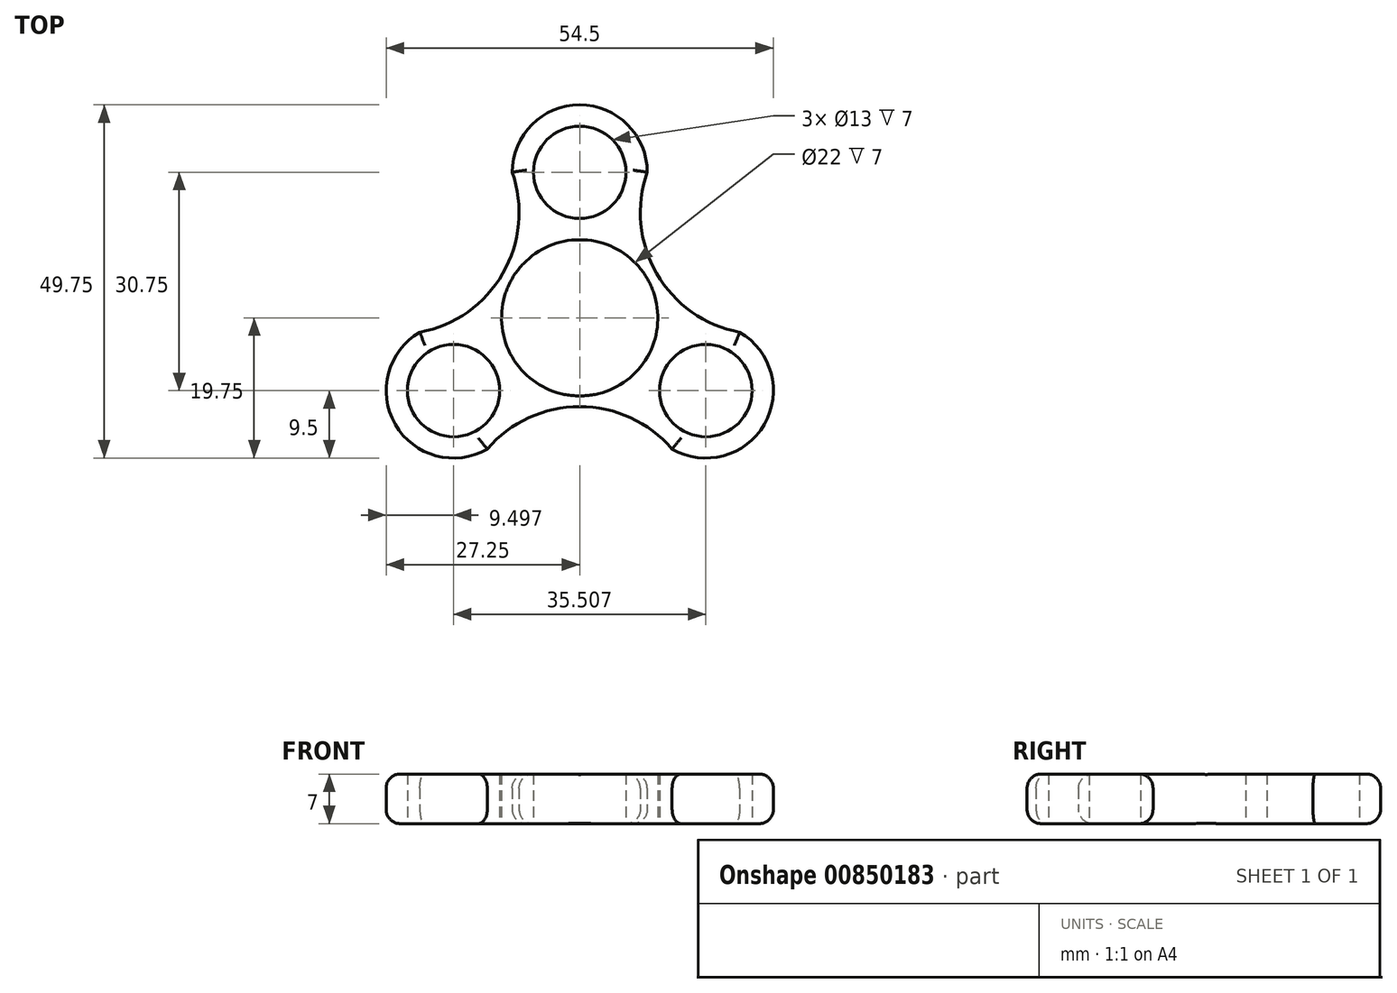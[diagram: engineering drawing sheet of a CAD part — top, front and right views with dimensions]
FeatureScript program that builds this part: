
annotation { "Feature Type Name" : "Feature", "Feature Type Description" : "" }
export const myFeature = defineFeature(function(context is Context, id is Id, definition is map)
    precondition{}
    {
        {
            var Q0;
            Q0=qCreatedBy(makeId("Top.planeOp"),FACE);
            var sketch = newSketch(context, id + "F0", { "sketchPlane" : qUnion([Q0])});
            skCircle(sketch, "E0", {"center": v(0, 0) * mm, "radius": 11 * mm});
            skCircle(sketch, "E1", {"center": v(0, 20.5) * mm, "radius": 6.5 * mm});
            skArc(sketch, "E2.0", {"start": v(9.5, 20.5) * mm, "mid": v(0, 30) * mm, "end": v(-9.5, 20.5) * mm});
            skCircle(sketch, "E3.1.1", {"center": v(-17.75, -10.25) * mm, "radius": 6.5 * mm});
            skCircle(sketch, "E3.2.1", {"center": v(17.75, -10.25) * mm, "radius": 6.5 * mm});
            skLineSegment(sketch, "E4", {"start": v(9.53, 5.5) * mm, "end": v(12.12, 7) * mm});
            skPoint(sketch, "E5", {"position": v(10.83, 6.25) * mm});
            skLineSegment(sketch, "E6.MirrorCS", {"start": v(17.75, -10.25) * mm, "end": v(18.88, -3.85) * mm});
            skLineSegment(sketch, "E7.MirrorCS", {"start": v(17.75, -10.25) * mm, "end": v(21, -4.62) * mm});
            skArc(sketch, "E8", {"start": v(9.5, 20.5) * mm, "mid": v(10.83, 6.25) * mm, "end": v(22.5, -2.02) * mm});
            skArc(sketch, "E9.1.0", {"start": v(-22.5, -2.02) * mm, "mid": v(-10.83, 6.25) * mm, "end": v(-9.5, 20.5) * mm});
            skArc(sketch, "E9.2.0", {"start": v(13, -18.48) * mm, "mid": v(0, -12.5) * mm, "end": v(-13, -18.48) * mm});
            skArc(sketch, "E10.trimOffspring", {"start": v(13, -18.48) * mm, "mid": v(25.98, -15) * mm, "end": v(22.5, -2.02) * mm});
            skArc(sketch, "E11.trimOffspring", {"start": v(-13.91, -1.56) * mm, "mid": v(-13.3, -4.37) * mm, "end": v(-12.12, -7) * mm});
            skArc(sketch, "E12.trimOffspring", {"start": v(-22.5, -2.02) * mm, "mid": v(-25.98, -15) * mm, "end": v(-13, -18.48) * mm});
            skLineSegment(sketch, "E13.trimOffspring", {"start": v(19.36, -1.12) * mm, "end": v(19.4, -0.9) * mm});
            skSolve(sketch);
        }
        {
            var Q0;
            {var subQ0=sQuery(id+"F0.wireOp",EDGE,"0f1f7083-71ca-4fd1-acfb-ab530d3e9b21.1.0");var subQ1=sQuery(id+"F0.wireOp",EDGE,"457ceb27-7422-4ba8-bad2-b165804d5d78.0");var subQ2=makeQuery(id+"F0.imprint","INTERSECT",VERTEX,{"derivedFrom":[subQ1,subQ0]});Q0=makeQuery(id+"F0.imprint","IMPRINT",FACE,{"disambiguationData":[TD([[makeQuery(id+"F0.imprint","IMPRINT",EDGE,{"disambiguationData":[TD([[subQ2,-1.0]])],"derivedFrom":subQ0}),-1.0]])]});}
            var Q1;
            {var subQ3=sQuery(id+"F0.wireOp",EDGE,"crWTvBME-xT62-r7Xz-G13u-5dXDQIS6QdV6");var subQ5=sQuery(id+"F0.wireOp",EDGE,"E1");var subQ6=makeQuery(id+"F0.imprint","INTERSECT",VERTEX,{"derivedFrom":[subQ5,subQ3]});Q1=makeQuery(id+"F0.imprint","IMPRINT",FACE,{"disambiguationData":[TD([[makeQuery(id+"F0.imprint","IMPRINT",EDGE,{"disambiguationData":[TD([[subQ6,1.0]])],"derivedFrom":subQ5}),-1.0]])]});}
            var Q2;
            {var subQ4=sQuery(id+"F0.wireOp",EDGE,"E1");var subQ7=sQuery(id+"F0.wireOp",EDGE,"crWTvBME-xT62-r7Xz-G13u-5dXDQIS6QdV6");var subQ9=makeQuery(id+"F0.imprint","INTERSECT",VERTEX,{"derivedFrom":[subQ4,subQ7]});Q2=makeQuery(id+"F0.imprint","IMPRINT",FACE,{"disambiguationData":[TD([[makeQuery(id+"F0.imprint","IMPRINT",EDGE,{"disambiguationData":[TD([[subQ9,-1.0]])],"derivedFrom":subQ4}),-1.0]])]});}
            var Q3;
            {var subQ0=sQuery(id+"F0.wireOp",EDGE,"FCme8Fqz-nV7u-H02u-gcTn-oEhTSx07MFKY");var subQ3=sQuery(id+"F0.wireOp",EDGE,"E2.0");var subQ5=makeQuery(id+"F0.imprint","INTERSECT",VERTEX,{"derivedFrom":[subQ3,subQ0]});Q3=makeQuery(id+"F0.imprint","IMPRINT",FACE,{"disambiguationData":[TD([[makeQuery(id+"F0.imprint","IMPRINT",EDGE,{"disambiguationData":[TD([[subQ5,1.0]])],"derivedFrom":subQ3}),-1.0]])]});}
            var Q4;
            {var subQ0=sQuery(id+"F0.wireOp",EDGE,"crWTvBME-xT62-r7Xz-G13u-5dXDQIS6QdV6");var subQ1=sQuery(id+"F0.wireOp",EDGE,"E0");var subQ2=makeQuery(id+"F0.imprint","INTERSECT",VERTEX,{"derivedFrom":[subQ1,subQ0]});Q4=makeQuery(id+"F0.imprint","IMPRINT",FACE,{"disambiguationData":[TD([[makeQuery(id+"F0.imprint","IMPRINT",EDGE,{"disambiguationData":[TD([[subQ2,1.0]])],"derivedFrom":subQ1}),-1.0]])]});}
            var Q5;
            {var subQ3=sQuery(id+"F0.wireOp",EDGE,"crWTvBME-xT62-r7Xz-G13u-5dXDQIS6QdV6");var subQ7=sQuery(id+"F0.wireOp",EDGE,"E0");var subQ9=makeQuery(id+"F0.imprint","INTERSECT",VERTEX,{"derivedFrom":[subQ7,subQ3]});Q5=makeQuery(id+"F0.imprint","IMPRINT",FACE,{"disambiguationData":[TD([[makeQuery(id+"F0.imprint","IMPRINT",EDGE,{"disambiguationData":[TD([[subQ9,-1.0]])],"derivedFrom":subQ7}),-1.0]])]});}
            var Q6;
            {var subQ0=sQuery(id+"F0.wireOp",EDGE,"0f1f7083-71ca-4fd1-acfb-ab530d3e9b21.1.0");var subQ1=sQuery(id+"F0.wireOp",EDGE,"457ceb27-7422-4ba8-bad2-b165804d5d78.0");var subQ2=makeQuery(id+"F0.imprint","INTERSECT",VERTEX,{"derivedFrom":[subQ1,subQ0]});Q6=makeQuery(id+"F0.imprint","IMPRINT",FACE,{"disambiguationData":[TD([[makeQuery(id+"F0.imprint","IMPRINT",EDGE,{"disambiguationData":[TD([[subQ2,-1.0]])],"derivedFrom":subQ1}),-1.0]])]});}
            var Q7;
            Q7=makeQuery(id+"F0.imprint","IMPRINT",FACE,{"disambiguationData":[TD([[makeQuery(id+"F0.imprint","IMPRINT",EDGE,{"derivedFrom":sQuery(id+"F0.wireOp",EDGE,"E3.1.1")}),-1.0]])]});
            var Q8;
            {var subQ0=sQuery(id+"F0.wireOp",EDGE,"0f1f7083-71ca-4fd1-acfb-ab530d3e9b21.2.0");var subQ1=sQuery(id+"F0.wireOp",EDGE,"457ceb27-7422-4ba8-bad2-b165804d5d78.0");var subQ2=makeQuery(id+"F0.imprint","INTERSECT",VERTEX,{"derivedFrom":[subQ1,subQ0]});Q8=makeQuery(id+"F0.imprint","IMPRINT",FACE,{"disambiguationData":[TD([[makeQuery(id+"F0.imprint","IMPRINT",EDGE,{"disambiguationData":[TD([[subQ2,1.0]])],"derivedFrom":subQ1}),-1.0]])]});}
            var Q9;
            {var subQ0=sQuery(id+"F0.wireOp",EDGE,"0f1f7083-71ca-4fd1-acfb-ab530d3e9b21.2.0");var subQ1=sQuery(id+"F0.wireOp",EDGE,"457ceb27-7422-4ba8-bad2-b165804d5d78.0");var subQ2=makeQuery(id+"F0.imprint","INTERSECT",VERTEX,{"derivedFrom":[subQ1,subQ0]});Q9=makeQuery(id+"F0.imprint","IMPRINT",FACE,{"disambiguationData":[TD([[makeQuery(id+"F0.imprint","IMPRINT",EDGE,{"disambiguationData":[TD([[subQ2,-1.0]])],"derivedFrom":subQ1}),-1.0]])]});}
            var Q10;
            Q10=makeQuery(id+"F0.imprint","IMPRINT",FACE,{"disambiguationData":[TD([[makeQuery(id+"F0.imprint","IMPRINT",EDGE,{"derivedFrom":sQuery(id+"F0.wireOp",EDGE,"E3.2.1")}),-1.0]])]});
            var Q11;
            {var subQ0=sQuery(id+"F0.wireOp",EDGE,"FCme8Fqz-nV7u-H02u-gcTn-oEhTSx07MFKY");var subQ3=sQuery(id+"F0.wireOp",EDGE,"E3.2.0");var subQ5=makeQuery(id+"F0.imprint","INTERSECT",VERTEX,{"disambiguationData":[OD(1.0)],"derivedFrom":[subQ3,subQ0]});Q11=makeQuery(id+"F0.imprint","IMPRINT",FACE,{"disambiguationData":[TD([[makeQuery(id+"F0.imprint","IMPRINT",EDGE,{"disambiguationData":[TD([[subQ5,-1.0]])],"derivedFrom":subQ3}),-1.0]])]});}
            var Q12;
            {var subQ0=sQuery(id+"F0.wireOp",EDGE,"Cn72uRpp-cvnh-8flW-uh67-CLD0QGApm8kP");var subQ1=sQuery(id+"F0.wireOp",EDGE,"457ceb27-7422-4ba8-bad2-b165804d5d78.0");var subQ2=makeQuery(id+"F0.imprint","INTERSECT",VERTEX,{"derivedFrom":[subQ1,sQuery(id+"F0.wireOp",EDGE,"E4"),subQ0]});Q12=makeQuery(id+"F0.imprint","IMPRINT",FACE,{"disambiguationData":[TD([[makeQuery(id+"F0.imprint","IMPRINT",EDGE,{"disambiguationData":[TD([[subQ2,-1.0]])],"derivedFrom":subQ1}),-1.0]])]});}
            var Q13;
            {var subQ0=sQuery(id+"F0.wireOp",EDGE,"crWTvBME-xT62-r7Xz-G13u-5dXDQIS6QdV6");Q13=makeQuery(id+"F0.imprint","IMPRINT",FACE,{"disambiguationData":[TD([[makeQuery(id+"F0.imprint","IMPRINT",EDGE,{"derivedFrom":subQ0}),-1.0]])]});}
            var Q14;
            {var subQ0=sQuery(id+"F0.wireOp",EDGE,"crWTvBME-xT62-r7Xz-G13u-5dXDQIS6QdV6");Q14=makeQuery(id+"F0.imprint","IMPRINT",FACE,{"disambiguationData":[TD([[makeQuery(id+"F0.imprint","IMPRINT",EDGE,{"derivedFrom":subQ0}),1.0]])]});}
            var Q15;
            {var subQ0=sQuery(id+"F0.wireOp",EDGE,"457ceb27-7422-4ba8-bad2-b165804d5d78.0");var subQ1=makeQuery(id+"F0.imprint","INTERSECT",VERTEX,{"derivedFrom":[subQ0,sQuery(id+"F0.wireOp",EDGE,"E3.1.1")]});Q15=makeQuery(id+"F0.imprint","IMPRINT",FACE,{"disambiguationData":[TD([[makeQuery(id+"F0.imprint","IMPRINT",EDGE,{"disambiguationData":[TD([[subQ1,1.0]])],"derivedFrom":subQ0}),1.0]])]});}
            var Q16;
            {var subQ0=sQuery(id+"F0.wireOp",EDGE,"E3.1.0");var subQ1=sQuery(id+"F0.wireOp",EDGE,"E0");var subQ2=makeQuery(id+"F0.imprint","INTERSECT",VERTEX,{"derivedFrom":[subQ1,subQ0]});Q16=makeQuery(id+"F0.imprint","IMPRINT",FACE,{"disambiguationData":[TD([[makeQuery(id+"F0.imprint","IMPRINT",EDGE,{"disambiguationData":[TD([[subQ2,-1.0]])],"derivedFrom":subQ1}),-1.0]])]});}
            var Q17;
            {var subQ0=sQuery(id+"F0.wireOp",EDGE,"b8a55ac8-5f56-46bf-a338-ef139d869b18.1.0");var subQ1=sQuery(id+"F0.wireOp",EDGE,"457ceb27-7422-4ba8-bad2-b165804d5d78.0");var subQ2=makeQuery(id+"F0.imprint","INTERSECT",VERTEX,{"derivedFrom":[subQ1,subQ0]});Q17=makeQuery(id+"F0.imprint","IMPRINT",FACE,{"disambiguationData":[TD([[makeQuery(id+"F0.imprint","IMPRINT",EDGE,{"disambiguationData":[TD([[subQ2,-1.0]])],"derivedFrom":subQ1}),-1.0]])]});}
            var Q18;
            {var subQ0=sQuery(id+"F0.wireOp",EDGE,"b8a55ac8-5f56-46bf-a338-ef139d869b18.2.0");var subQ1=sQuery(id+"F0.wireOp",EDGE,"457ceb27-7422-4ba8-bad2-b165804d5d78.0");var subQ2=makeQuery(id+"F0.imprint","INTERSECT",VERTEX,{"derivedFrom":[subQ1,subQ0]});Q18=makeQuery(id+"F0.imprint","IMPRINT",FACE,{"disambiguationData":[TD([[makeQuery(id+"F0.imprint","IMPRINT",EDGE,{"disambiguationData":[TD([[subQ2,1.0]])],"derivedFrom":subQ1}),-1.0]])]});}
            var Q19;
            {var subQ0=sQuery(id+"F0.wireOp",EDGE,"b8a55ac8-5f56-46bf-a338-ef139d869b18.2.0");var subQ1=sQuery(id+"F0.wireOp",EDGE,"457ceb27-7422-4ba8-bad2-b165804d5d78.0");var subQ2=makeQuery(id+"F0.imprint","INTERSECT",VERTEX,{"derivedFrom":[subQ1,subQ0]});Q19=makeQuery(id+"F0.imprint","IMPRINT",FACE,{"disambiguationData":[TD([[makeQuery(id+"F0.imprint","IMPRINT",EDGE,{"disambiguationData":[TD([[subQ2,-1.0]])],"derivedFrom":subQ1}),-1.0]])]});}
            var Q20;
            {var subQ0=sQuery(id+"F0.wireOp",EDGE,"E3.2.0");var subQ1=sQuery(id+"F0.wireOp",EDGE,"457ceb27-7422-4ba8-bad2-b165804d5d78.0");var subQ2=makeQuery(id+"F0.imprint","INTERSECT",VERTEX,{"disambiguationData":[OD(0.0)],"derivedFrom":[subQ1,subQ0]});Q20=makeQuery(id+"F0.imprint","IMPRINT",FACE,{"disambiguationData":[TD([[makeQuery(id+"F0.imprint","IMPRINT",EDGE,{"disambiguationData":[TD([[subQ2,-1.0]])],"derivedFrom":subQ1}),1.0]])]});}
            var Q21;
            {var subQ1=sQuery(id+"F0.wireOp",EDGE,"457ceb27-7422-4ba8-bad2-b165804d5d78.0");var subQ3=sQuery(id+"F0.wireOp",EDGE,"E3.2.0");var subQ4=makeQuery(id+"F0.imprint","INTERSECT",VERTEX,{"disambiguationData":[OD(1.0)],"derivedFrom":[subQ1,subQ3]});Q21=makeQuery(id+"F0.imprint","IMPRINT",FACE,{"disambiguationData":[TD([[makeQuery(id+"F0.imprint","IMPRINT",EDGE,{"disambiguationData":[TD([[subQ4,-1.0]])],"derivedFrom":subQ1}),-1.0]])]});}
            var Q22;
            {var subQ1=sQuery(id+"F0.wireOp",EDGE,"E3.2.0");var subQ4=sQuery(id+"F0.wireOp",EDGE,"457ceb27-7422-4ba8-bad2-b165804d5d78.0");var subQ5=makeQuery(id+"F0.imprint","INTERSECT",VERTEX,{"disambiguationData":[OD(0.0)],"derivedFrom":[subQ4,subQ1]});Q22=makeQuery(id+"F0.imprint","IMPRINT",FACE,{"disambiguationData":[TD([[makeQuery(id+"F0.imprint","IMPRINT",EDGE,{"disambiguationData":[TD([[subQ5,-1.0]])],"derivedFrom":subQ4}),-1.0]])]});}
            extrude(context, id + "F1", {"entities" : qUnion([Q0, Q1, Q2, Q3, Q4, Q5, Q6, Q7, Q8, Q9, Q10, Q11, Q12, Q13, Q14, Q15, Q16, Q17, Q18, Q19, Q20, Q21, Q22]), "depth" : 7 * mm, "offsetDistance" : 25 * mm});
        }
        {
            var Q0;
            Q0=makeQuery(id+"F1.opExtrude","CAP_EDGE",EDGE,{"disambiguationData":[OSD([sQuery(id+"F0.wireOp",EDGE,"b8a55ac8-5f56-46bf-a338-ef139d869b18.1.0")])],"isStart":false});
            var Q1;
            {var subQ0=sQuery(id+"F0.wireOp",EDGE,"E2.0");Q1=makeQuery(id+"F1.opExtrude","CAP_EDGE",EDGE,{"disambiguationData":[OSD([subQ0]),TDD([makeQuery(id+"F0.imprint","IMPRINT",EDGE,{"disambiguationData":[TD([[makeQuery(id+"F0.imprint","INTERSECT",VERTEX,{"derivedFrom":[subQ0,sQuery(id+"F0.wireOp",EDGE,"b8a55ac8-5f56-46bf-a338-ef139d869b18.1.0")]}),1.0]])],"derivedFrom":subQ0})])],"isStart":false});}
            var Q2;
            Q2=makeQuery(id+"F1.opExtrude","CAP_EDGE",EDGE,{"disambiguationData":[OSD([sQuery(id+"F0.wireOp",EDGE,"Cn72uRpp-cvnh-8flW-uh67-CLD0QGApm8kP")])],"isStart":false});
            var Q3;
            {var subQ0=sQuery(id+"F0.wireOp",EDGE,"E3.2.0");Q3=makeQuery(id+"F1.opExtrude","CAP_EDGE",EDGE,{"disambiguationData":[OSD([subQ0]),TDD([makeQuery(id+"F0.imprint","IMPRINT",EDGE,{"disambiguationData":[TD([[makeQuery(id+"F0.imprint","INTERSECT",VERTEX,{"derivedFrom":[subQ0,sQuery(id+"F0.wireOp",EDGE,"Cn72uRpp-cvnh-8flW-uh67-CLD0QGApm8kP")]}),1.0]])],"derivedFrom":subQ0})])],"isStart":false});}
            var Q4;
            Q4=makeQuery(id+"F1.opExtrude","CAP_EDGE",EDGE,{"disambiguationData":[OSD([sQuery(id+"F0.wireOp",EDGE,"b8a55ac8-5f56-46bf-a338-ef139d869b18.2.0")])],"isStart":false});
            var Q5;
            {var subQ0=sQuery(id+"F0.wireOp",EDGE,"E3.1.0");Q5=makeQuery(id+"F1.opExtrude","CAP_EDGE",EDGE,{"disambiguationData":[OSD([subQ0]),TDD([makeQuery(id+"F0.imprint","IMPRINT",EDGE,{"disambiguationData":[TD([[makeQuery(id+"F0.imprint","INTERSECT",VERTEX,{"derivedFrom":[subQ0,sQuery(id+"F0.wireOp",EDGE,"b8a55ac8-5f56-46bf-a338-ef139d869b18.1.0")]}),-1.0]])],"derivedFrom":subQ0})])],"isStart":false});}
            var Q6;
            Q6=makeQuery(id+"F1.opExtrude","CAP_EDGE",EDGE,{"disambiguationData":[OSD([sQuery(id+"F0.wireOp",EDGE,"b8a55ac8-5f56-46bf-a338-ef139d869b18.1.0")])],"isStart":true});
            var Q7;
            {var subQ0=sQuery(id+"F0.wireOp",EDGE,"E3.1.0");Q7=makeQuery(id+"F1.opExtrude","CAP_EDGE",EDGE,{"disambiguationData":[OSD([subQ0]),TDD([makeQuery(id+"F0.imprint","IMPRINT",EDGE,{"disambiguationData":[TD([[makeQuery(id+"F0.imprint","INTERSECT",VERTEX,{"derivedFrom":[subQ0,sQuery(id+"F0.wireOp",EDGE,"b8a55ac8-5f56-46bf-a338-ef139d869b18.1.0")]}),-1.0]])],"derivedFrom":subQ0})])],"isStart":true});}
            var Q8;
            Q8=makeQuery(id+"F1.opExtrude","CAP_EDGE",EDGE,{"disambiguationData":[OSD([sQuery(id+"F0.wireOp",EDGE,"b8a55ac8-5f56-46bf-a338-ef139d869b18.2.0")])],"isStart":true});
            var Q9;
            {var subQ0=sQuery(id+"F0.wireOp",EDGE,"E3.2.0");Q9=makeQuery(id+"F1.opExtrude","CAP_EDGE",EDGE,{"disambiguationData":[OSD([subQ0]),TDD([makeQuery(id+"F0.imprint","IMPRINT",EDGE,{"disambiguationData":[TD([[makeQuery(id+"F0.imprint","INTERSECT",VERTEX,{"derivedFrom":[subQ0,sQuery(id+"F0.wireOp",EDGE,"Cn72uRpp-cvnh-8flW-uh67-CLD0QGApm8kP")]}),1.0]])],"derivedFrom":subQ0})])],"isStart":true});}
            var Q10;
            Q10=makeQuery(id+"F1.opExtrude","CAP_EDGE",EDGE,{"disambiguationData":[OSD([sQuery(id+"F0.wireOp",EDGE,"Cn72uRpp-cvnh-8flW-uh67-CLD0QGApm8kP")])],"isStart":true});
            var Q11;
            {var subQ0=sQuery(id+"F0.wireOp",EDGE,"E2.0");Q11=makeQuery(id+"F1.opExtrude","CAP_EDGE",EDGE,{"disambiguationData":[OSD([subQ0]),TDD([makeQuery(id+"F0.imprint","IMPRINT",EDGE,{"disambiguationData":[TD([[makeQuery(id+"F0.imprint","INTERSECT",VERTEX,{"derivedFrom":[subQ0,sQuery(id+"F0.wireOp",EDGE,"b8a55ac8-5f56-46bf-a338-ef139d869b18.1.0")]}),1.0]])],"derivedFrom":subQ0})])],"isStart":true});}
            var Q12;
            Q12=makeQuery(id+"F1.opExtrude","CAP_EDGE",EDGE,{"disambiguationData":[OSD([sQuery(id+"F0.wireOp",EDGE,"E9.1.0")])],"isStart":false});
            var Q13;
            Q13=makeQuery(id+"F1.opExtrude","CAP_EDGE",EDGE,{"disambiguationData":[OSD([sQuery(id+"F0.wireOp",EDGE,"E12.trimOffspring")])],"isStart":false});
            var Q14;
            Q14=makeQuery(id+"F1.opExtrude","CAP_EDGE",EDGE,{"disambiguationData":[OSD([sQuery(id+"F0.wireOp",EDGE,"E9.2.0")])],"isStart":false});
            var Q15;
            Q15=makeQuery(id+"F1.opExtrude","CAP_EDGE",EDGE,{"disambiguationData":[OSD([sQuery(id+"F0.wireOp",EDGE,"E10.trimOffspring")])],"isStart":false});
            var Q16;
            Q16=makeQuery(id+"F1.opExtrude","CAP_EDGE",EDGE,{"disambiguationData":[OSD([sQuery(id+"F0.wireOp",EDGE,"E8")])],"isStart":false});
            var Q17;
            Q17=makeQuery(id+"F1.opExtrude","CAP_EDGE",EDGE,{"disambiguationData":[OSD([sQuery(id+"F0.wireOp",EDGE,"E9.1.0")])],"isStart":true});
            var Q18;
            Q18=makeQuery(id+"F1.opExtrude","CAP_EDGE",EDGE,{"disambiguationData":[OSD([sQuery(id+"F0.wireOp",EDGE,"E12.trimOffspring")])],"isStart":true});
            var Q19;
            Q19=makeQuery(id+"F1.opExtrude","CAP_EDGE",EDGE,{"disambiguationData":[OSD([sQuery(id+"F0.wireOp",EDGE,"E9.2.0")])],"isStart":true});
            var Q20;
            Q20=makeQuery(id+"F1.opExtrude","CAP_EDGE",EDGE,{"disambiguationData":[OSD([sQuery(id+"F0.wireOp",EDGE,"E10.trimOffspring")])],"isStart":true});
            var Q21;
            Q21=makeQuery(id+"F1.opExtrude","CAP_EDGE",EDGE,{"disambiguationData":[OSD([sQuery(id+"F0.wireOp",EDGE,"E8")])],"isStart":true});
            fillet(context, id + "F2", {"entities" : qUnion([Q0, Q1, Q2, Q3, Q4, Q5, Q6, Q7, Q8, Q9, Q10, Q11, Q12, Q13, Q14, Q15, Q16, Q17, Q18, Q19, Q20, Q21]), "radius" : 2 * mm, "tangentPropagation" : true, "allowEdgeOverflow" : false});
        }
    });
